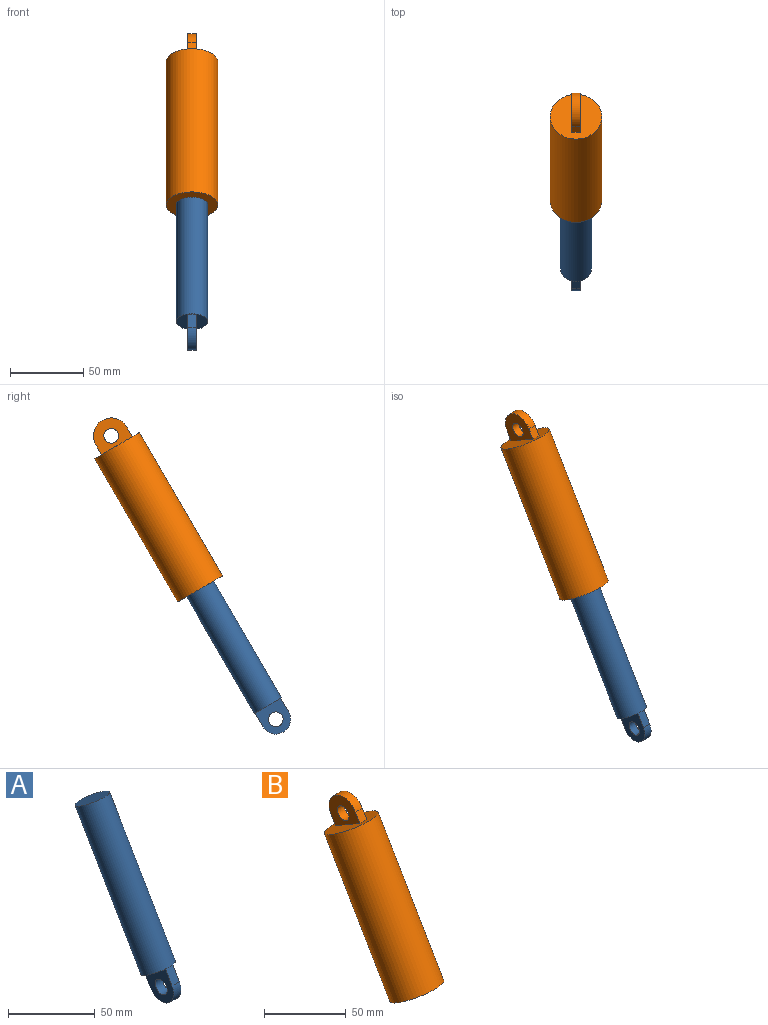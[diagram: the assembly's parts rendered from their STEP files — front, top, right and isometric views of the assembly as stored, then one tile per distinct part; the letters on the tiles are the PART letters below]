
ASSEMBLY  parts=2 mates=1
PART A: 9 faces, bbox 21.3x78.5x117.3 mm
  f0: cylinder r=10.65mm len=103.23mm, axis (0,0.5,0.86), area 7159.3mm2, adj f1,f2
  f1: plane 21.3x18.42mm, normal (0,-0.5,-0.86), area 234.9mm2, adj f0,f3,f6,f7,f8
  f2: plane 21.3x18.42mm, normal (0,0.5,0.86), area 356.3mm2, adj f0
  f3: plane 9.3x6mm, normal (0,-0.86,0.5), area 64.5mm2, adj f1,f4,f7,f8
  f4: cylinder r=10.11mm len=18.86mm, axis (-1,0,0), area 190.7mm2, adj f3,f6,f7,f8
  f5: cylinder r=5mm len=10mm, axis (-1,0,0), area 188.5mm2, adj f7,f8
  f6: plane 9.3x6mm, normal (0,0.86,-0.5), area 64.5mm2, adj f1,f4,f7,f8
  f7: plane 24.5x24.26mm, normal (1,0,0), area 299.8mm2, adj f1,f3,f4,f5,f6
  f8: plane 24.5x24.26mm, normal (-1,0,0), area 299.8mm2, adj f1,f3,f4,f5,f6
PART B: 15 faces, bbox 35.3x88.1x125.5 mm
  f0: plane 17.67x10.26mm, normal (0,-0.5,-0.86), area 115.1mm2, adj f1,f6
  f1: cylinder r=10.65mm len=104.18mm, axis (0,-0.5,-0.86), area 7031.4mm2, adj f0,f4,f5,f6,f7,f8
  f2: cylinder r=17.66mm len=115.46mm, axis (0,-0.5,-0.86), area 12539.8mm2, adj f3,f4
  f3: plane 35.32x30.55mm, normal (0,0.5,0.86), area 833.8mm2, adj f2,f9,f10,f11,f12
  f4: plane 35.32x30.55mm, normal (0,-0.5,-0.86), area 623.7mm2, adj f1,f2
  f5: plane 17.67x10.26mm, normal (0,-0.5,-0.86), area 115.1mm2, adj f1,f7
  f6: plane 26.03x24.52mm, normal (-1,0,0), area 338.5mm2, adj f0,f1,f8
  f7: plane 26.03x24.52mm, normal (1,0,0), area 338.5mm2, adj f1,f5,f8
  f8: plane 18.5x10.56mm, normal (0,-0.5,-0.87), area 126.1mm2, adj f1,f6,f7
  f9: plane 6.75x6mm, normal (0,0.86,-0.5), area 46.9mm2, adj f3,f11,f12,f13
  f10: plane 6.75x6mm, normal (0,-0.86,0.5), area 46.9mm2, adj f3,f11,f12,f13
  f11: plane 26.63x25.05mm, normal (1,0,0), area 344.6mm2, adj f3,f9,f10,f13,f14
  f12: plane 26.63x25.05mm, normal (-1,0,0), area 344.6mm2, adj f3,f9,f10,f13,f14
  f13: cylinder r=12.18mm len=22.71mm, axis (-1,0,0), area 229.6mm2, adj f9,f10,f11,f12
  f14: cylinder r=5mm len=10mm, axis (-1,0,0), area 188.5mm2, adj f11,f12
PLACE A rot(axis=(0.31,0.94,0.1),0deg) t=(37.3,47.97,-4.92)mm
PLACE B rot(axis=(0.31,0.94,0.1),0deg) t=(37.3,45.99,-8.33)mm
MATE slider A.f0 <-> B.f1  axis (0,0.5,0.86) through (71.3,126.28,129.96)mm
